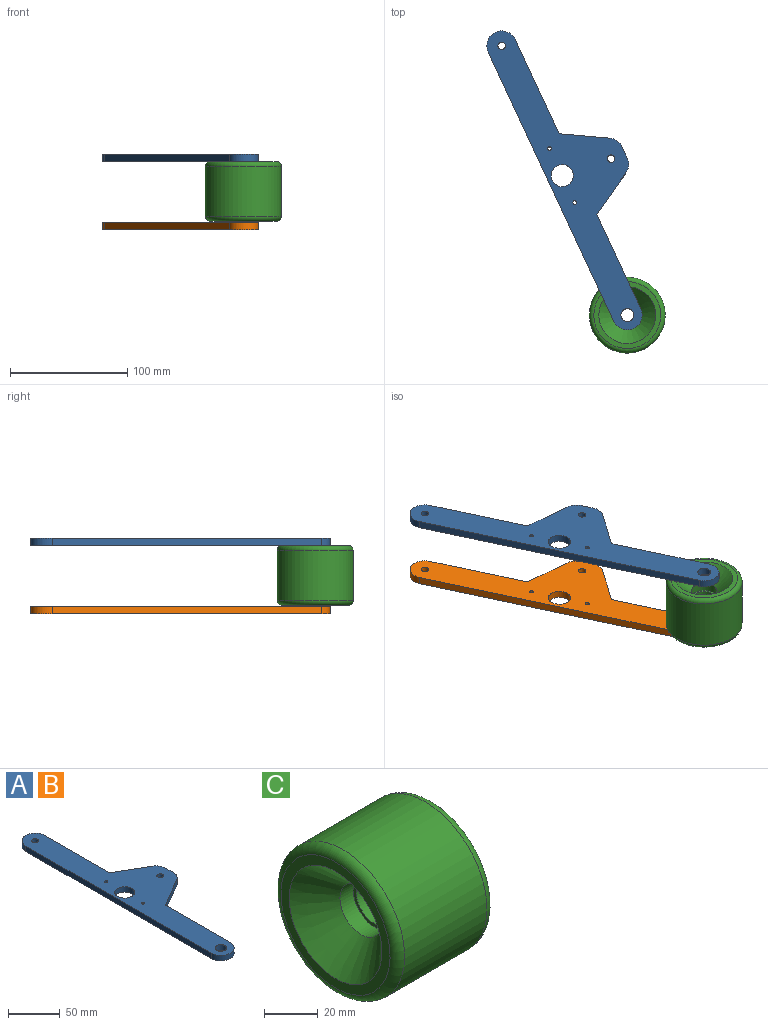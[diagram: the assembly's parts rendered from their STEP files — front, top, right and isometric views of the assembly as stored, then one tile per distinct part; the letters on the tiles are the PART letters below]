
ASSEMBLY  parts=3 mates=3
PART A: 18 faces, bbox 69.4x279.4x6.4 mm
  f0: plane 37.64x21.73mm, normal (0.5,0.87,0), area 276mm2, adj f1,f14,f16,f17
  f1: plane 88.9x6.35mm, normal (1,0,0), area 564.5mm2, adj f0,f2,f16,f17
  f2: cylinder r=12.7mm len=25.4mm, axis (0,0,-1), area 253.4mm2, adj f1,f3,f16,f17
  f3: plane 254x6.35mm, normal (-1,0,0), area 1612.9mm2, adj f2,f4,f16,f17
  f4: cylinder r=12.7mm len=25.4mm, axis (0,0,-1), area 253.4mm2, adj f3,f5,f16,f17
  f5: plane 88.9x6.35mm, normal (1,0,0), area 564.5mm2, adj f4,f6,f16,f17
  f6: plane 37.64x21.73mm, normal (0.5,-0.87,0), area 276mm2, adj f5,f7,f16,f17
  f7: cylinder r=12.7mm len=11mm, axis (0,0,-1), area 84.5mm2, adj f6,f8,f16,f17
  f8: plane 10.74x6.35mm, normal (1,0,0), area 68.2mm2, adj f7,f14,f16,f17
  f9: cylinder r=1.59mm len=6.35mm, axis (0,0,-1), area 63.3mm2, adj f16,f17
  f10: cylinder r=1.59mm len=6.35mm, axis (0,0,-1), area 63.3mm2, adj f16,f17
  f11: cylinder r=5.5mm len=11mm, axis (0,0,-1), area 219.4mm2, adj f16,f17
  f12: cylinder r=9.53mm len=19.05mm, axis (0,0,-1), area 380mm2, adj f16,f17
  f13: cylinder r=3.17mm len=6.35mm, axis (0,0,-1), area 126.7mm2, adj f16,f17
  f14: cylinder r=12.7mm len=11mm, axis (0,0,-1), area 84.5mm2, adj f0,f8,f16,f17
  f15: cylinder r=3.17mm len=6.35mm, axis (0,0,-1), area 126.7mm2, adj f16,f17
  f16: plane 279.4x69.39mm, normal (0,0,1), area 8716.6mm2, adj f0,f1,f2,f3,f4,f5,f6,f7
  f17: plane 279.4x69.39mm, normal (0,0,-1), area 8716.6mm2, adj f0,f1,f2,f3,f4,f5,f6,f7
PART B: same geometry as A
PART C: 12 faces, bbox 50.8x70.1x70.1 mm
  f0: cylinder r=32.38mm len=64.77mm, axis (-1,0,0), area 8786.3mm2, adj f1,f11
  f1: torus R=28.57mm, axis (-1,0,0), area 1165.7mm2, adj f0,f2
  f2: plane 57.15x57.15mm, normal (-1,0,0), area 708.9mm2, adj f1,f3
  f3: cone r=24.31mm half-angle=45deg, axis (-1,0,0), area 2087.7mm2, adj f2,f4
  f4: cylinder r=11mm len=22mm, axis (-1,0,0), area 484.4mm2, adj f3,f5
  f5: plane 22x22mm, normal (-1,0,0), area 98mm2, adj f4,f6
  f6: cylinder r=9.47mm len=18.95mm, axis (-1,0,0), area 604.8mm2, adj f5,f7
  f7: plane 22x22mm, normal (1,0,0), area 98mm2, adj f6,f8
  f8: cylinder r=11mm len=22mm, axis (-1,0,0), area 484.4mm2, adj f7,f9
  f9: cone r=24.31mm half-angle=45deg, axis (1,0,0), area 2087.7mm2, adj f8,f10
  f10: plane 57.15x57.15mm, normal (1,0,0), area 708.9mm2, adj f9,f11
  f11: torus R=28.57mm, axis (-1,0,0), area 1165.7mm2, adj f0,f10
PLACE A rot(axis=(0,0,1),25deg) t=(109.83,-81.11,-6.88)mm
PLACE B rot(axis=(0,0,1),25deg) t=(109.83,-81.11,-65.46)mm
PLACE C rot(axis=(-0.71,-0.05,-0.71),174.8deg) t=(175.01,-190.84,-32.48)mm
MATE planar A.f1 <-> B.f1  axis (0.91,0.42,0) through (97.96,4.44,-6.88)mm
MATE revolute C.f0 <-> B.f4  axis (0,0,-1) through (175.01,-190.84,-57.84)mm
MATE revolute C.f0 <-> A.f4  axis (0,0,-1) through (175.01,-190.84,-8.15)mm
